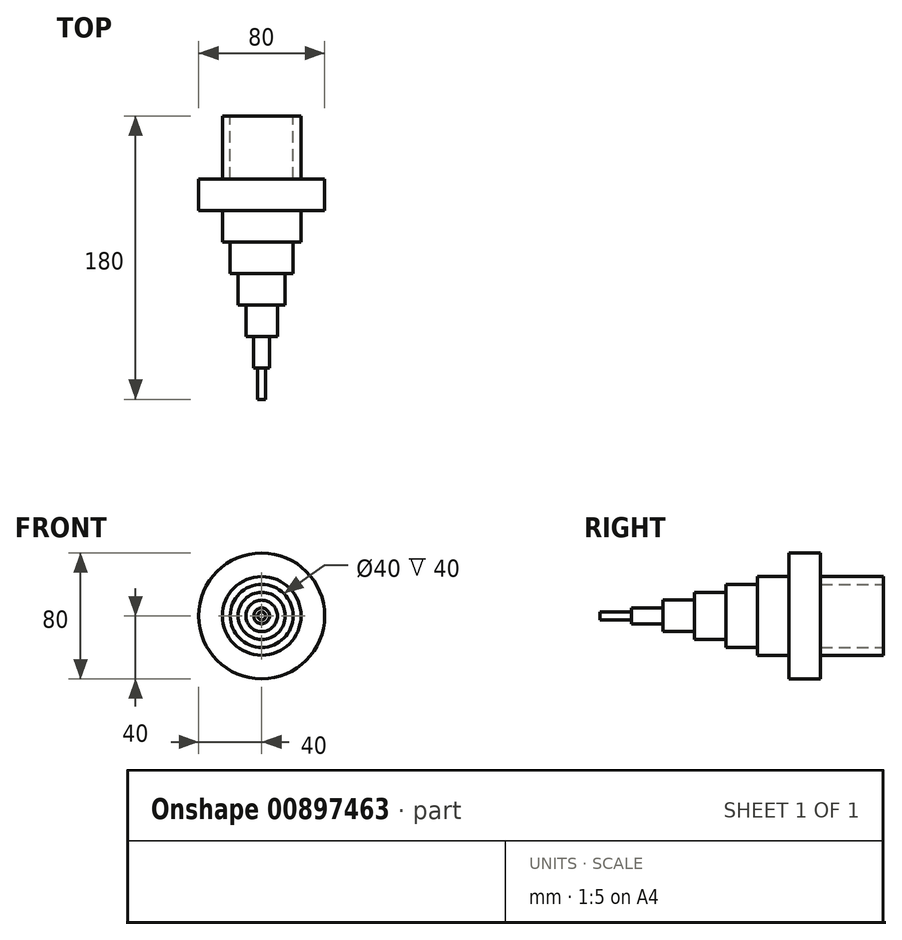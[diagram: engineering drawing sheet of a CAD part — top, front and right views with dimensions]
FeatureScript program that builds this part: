
annotation { "Feature Type Name" : "Feature", "Feature Type Description" : "" }
export const myFeature = defineFeature(function(context is Context, id is Id, definition is map)
    precondition{}
    {
        {
            var Q0;
            Q0=qCreatedBy(makeId("Front.planeOp"),FACE);
            var sketch = newSketch(context, id + "F0", { "sketchPlane" : qUnion([Q0])});
            skCircle(sketch, "E0", {"center": v(0, 0) * mm, "radius": 40 * mm});
            skSolve(sketch);
        }
        {
            var Q0;
            Q0=makeQuery(id+"F0.imprint","IMPRINT",FACE,{"disambiguationData":[TD([[makeQuery(id+"F0.imprint","IMPRINT",EDGE,{"derivedFrom":sQuery(id+"F0.wireOp",EDGE,"E0")}),1.0]])]});
            extrude(context, id + "F1", {"entities" : qUnion([Q0]), "depth" : 20 * mm, "offsetDistance" : 25.4 * mm});
        }
        {
            var Q0;
            Q0=makeQuery(id+"F1.opExtrude","CAP_FACE",FACE,{"disambiguationData":[OSD([sQuery(id+"F0.wireOp",EDGE,"E0")])],"isStart":false});
            var sketch = newSketch(context, id + "F2", { "sketchPlane" : qUnion([Q0])});
            skCircle(sketch, "E1", {"center": v(0, 0) * mm, "radius": 25 * mm});
            skSolve(sketch);
        }
        {
            var Q0;
            Q0=makeQuery(id+"F2.imprint","IMPRINT",FACE,{"disambiguationData":[TD([[makeQuery(id+"F2.imprint","IMPRINT",EDGE,{"derivedFrom":sQuery(id+"F2.wireOp",EDGE,"E1")}),1.0]])]});
            extrude(context, id + "F3", {"entities" : qUnion([Q0]), "operationType" : NewBodyOperationType.ADD, "depth" : 20 * mm, "offsetDistance" : 25.4 * mm});
        }
        {
            var Q0;
            Q0=makeQuery(id+"F3.opExtrude","CAP_FACE",FACE,{"disambiguationData":[OSD([sQuery(id+"F2.wireOp",EDGE,"E1")])],"isStart":false});
            var sketch = newSketch(context, id + "F4", { "sketchPlane" : qUnion([Q0])});
            skCircle(sketch, "E2", {"center": v(0, 0) * mm, "radius": 20 * mm});
            skSolve(sketch);
        }
        {
            var Q0;
            Q0=makeQuery(id+"F4.imprint","IMPRINT",FACE,{"disambiguationData":[TD([[makeQuery(id+"F4.imprint","IMPRINT",EDGE,{"derivedFrom":sQuery(id+"F4.wireOp",EDGE,"E2")}),1.0]])]});
            extrude(context, id + "F5", {"entities" : qUnion([Q0]), "operationType" : NewBodyOperationType.ADD, "depth" : 20 * mm, "offsetDistance" : 25.4 * mm});
        }
        {
            var Q0;
            Q0=makeQuery(id+"F5.opExtrude","CAP_FACE",FACE,{"disambiguationData":[OSD([sQuery(id+"F4.wireOp",EDGE,"E2")])],"isStart":false});
            var sketch = newSketch(context, id + "F6", { "sketchPlane" : qUnion([Q0])});
            skCircle(sketch, "E3", {"center": v(0, 0) * mm, "radius": 15 * mm});
            skSolve(sketch);
        }
        {
            var Q0;
            Q0=makeQuery(id+"F6.imprint","IMPRINT",FACE,{"disambiguationData":[TD([[makeQuery(id+"F6.imprint","IMPRINT",EDGE,{"derivedFrom":sQuery(id+"F6.wireOp",EDGE,"E3")}),1.0]])]});
            extrude(context, id + "F7", {"entities" : qUnion([Q0]), "operationType" : NewBodyOperationType.ADD, "depth" : 20 * mm, "offsetDistance" : 25.4 * mm});
        }
        {
            var Q0;
            Q0=makeQuery(id+"F7.opExtrude","CAP_FACE",FACE,{"disambiguationData":[OSD([sQuery(id+"F6.wireOp",EDGE,"E3")])],"isStart":false});
            var sketch = newSketch(context, id + "F8", { "sketchPlane" : qUnion([Q0])});
            skCircle(sketch, "E4", {"center": v(0, 0) * mm, "radius": 10 * mm});
            skSolve(sketch);
        }
        {
            var Q0;
            Q0=makeQuery(id+"F8.imprint","IMPRINT",FACE,{"disambiguationData":[TD([[makeQuery(id+"F8.imprint","IMPRINT",EDGE,{"derivedFrom":sQuery(id+"F8.wireOp",EDGE,"E4")}),1.0]])]});
            var Q1;
            Q1 = qSketchRegion(id + "F10", true);
            var Q2;
            Q2 = qSketchRegion(id + "F12", true);
            extrude(context, id + "F9", {"entities" : qUnion([Q0, Q1, Q2]), "operationType" : NewBodyOperationType.ADD, "depth" : 20 * mm, "offsetDistance" : 25.4 * mm});
        }
        {
            var Q0;
            Q0=makeQuery(id+"F9.opExtrude","CAP_FACE",FACE,{"disambiguationData":[OSD([sQuery(id+"F8.wireOp",EDGE,"E4")])],"isStart":false});
            var sketch = newSketch(context, id + "F10", { "sketchPlane" : qUnion([Q0])});
            skCircle(sketch, "E5", {"center": v(0, 0) * mm, "radius": 5 * mm});
            skSolve(sketch);
        }
        {
            var Q0;
            Q0=makeQuery(id+"F10.imprint","IMPRINT",FACE,{"disambiguationData":[TD([[makeQuery(id+"F10.imprint","IMPRINT",EDGE,{"derivedFrom":sQuery(id+"F10.wireOp",EDGE,"E5")}),1.0]])]});
            extrude(context, id + "F11", {"entities" : qUnion([Q0]), "operationType" : NewBodyOperationType.ADD, "depth" : 20 * mm, "offsetDistance" : 25.4 * mm});
        }
        {
            var Q0;
            Q0=makeQuery(id+"F11.opExtrude","CAP_FACE",FACE,{"disambiguationData":[OSD([sQuery(id+"F10.wireOp",EDGE,"E5")])],"isStart":false});
            var sketch = newSketch(context, id + "F12", { "sketchPlane" : qUnion([Q0])});
            skCircle(sketch, "E6", {"center": v(0, 0) * mm, "radius": 2.5 * mm});
            skSolve(sketch);
        }
        {
            var Q0;
            Q0=makeQuery(id+"F12.imprint","IMPRINT",FACE,{"disambiguationData":[TD([[makeQuery(id+"F12.imprint","IMPRINT",EDGE,{"derivedFrom":sQuery(id+"F12.wireOp",EDGE,"E6")}),1.0]])]});
            extrude(context, id + "F13", {"entities" : qUnion([Q0]), "operationType" : NewBodyOperationType.ADD, "depth" : 20 * mm, "offsetDistance" : 25.4 * mm});
        }
        {
            var Q0;
            Q0=makeQuery(id+"F1.opExtrude","CAP_FACE",FACE,{"disambiguationData":[OSD([sQuery(id+"F0.wireOp",EDGE,"E0")])],"isStart":true});
            var sketch = newSketch(context, id + "F14", { "sketchPlane" : qUnion([Q0])});
            skCircle(sketch, "E7", {"center": v(0, 0) * mm, "radius": 25 * mm});
            skSolve(sketch);
        }
        {
            var Q0;
            Q0=makeQuery(id+"F14.imprint","IMPRINT",FACE,{"disambiguationData":[TD([[makeQuery(id+"F14.imprint","IMPRINT",EDGE,{"derivedFrom":sQuery(id+"F14.wireOp",EDGE,"E7")}),1.0]])]});
            extrude(context, id + "F15", {"entities" : qUnion([Q0]), "operationType" : NewBodyOperationType.ADD, "depth" : 40 * mm, "offsetDistance" : 25.4 * mm});
        }
        {
            var Q0;
            Q0=makeQuery(id+"F15.opExtrude","CAP_FACE",FACE,{"disambiguationData":[OSD([sQuery(id+"F14.wireOp",EDGE,"E7")])],"isStart":false});
            var sketch = newSketch(context, id + "F16", { "sketchPlane" : qUnion([Q0])});
            skCircle(sketch, "E8", {"center": v(0, 0) * mm, "radius": 20 * mm});
            skSolve(sketch);
        }
        {
            var Q0;
            Q0=makeQuery(id+"F16.imprint","IMPRINT",FACE,{"disambiguationData":[TD([[makeQuery(id+"F16.imprint","IMPRINT",EDGE,{"derivedFrom":sQuery(id+"F16.wireOp",EDGE,"E8")}),1.0]])]});
            extrude(context, id + "F17", {"entities" : qUnion([Q0]), "operationType" : NewBodyOperationType.REMOVE, "oppositeDirection" : true, "depth" : 40 * mm, "offsetDistance" : 25.4 * mm});
        }
    });
